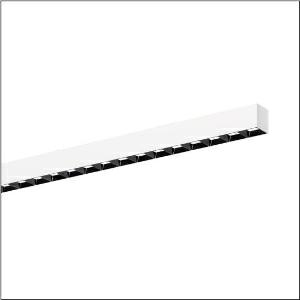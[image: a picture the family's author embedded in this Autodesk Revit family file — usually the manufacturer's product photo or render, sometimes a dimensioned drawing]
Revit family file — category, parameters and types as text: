
# Revit family: silica_r__21_51mx24tbt5w_c5f4
name_source: partatom
category: Lighting Fixtures
units: mm (PartAtom-declared; Revit-internal decimal feet)

## family parameters
Cut with Voids When Loaded = No
Host = Face
Light Source = No
Part Type = Normal
Room Calculation Point = No
Round Connector Dimension = Use Diameter
Shared = No

## types (1)
- --- (1 x LED, 4100 lm, 40.5 W, 6500K)
    Apparent Load = 41 VA
    CIE Flux Codes = 74 94 99 100 100
    Color Rendering = 80
    Color Temperature = 6500K
    Default Elevation = 1800 mm
    Description = Silica® 21, office luminaire, primary light control with darklight reflector, of PMMA, black, light emission: direct distribution, primary light characteristic: asymmetric, installation type: surface-mounted, LED, rated luminous flux: 4.100lm, luminous efficacy: 96lm/W, light colour: 8tw, colour temperature: 2700..6500K, control gear: ECG DALI, with terminal, 3+2-pole, max. 2.5mm², mains connection: 220..240V, AC, 50/60Hz, rated input power: 42.6W, luminaire housing, of aluminium, traffic white (RAL 9016), length: 1.504mm, width: 53mm, height: 53mm, protection rating (complete): IP20, insulation class (complete): insulation class I (protective earthing), certification: CE, permissible operating ambient temperature: 0..+35°C, standard: EN 50419, packaging unit: 1 piece
    Height = 0 mm  [stored 0 ft]
    Lamp = 1 x LED
    Lamp Light Flux = 4100 lm
    Lamp Power = 40.5 W
    Lamp count = 1
    Length = 1504 mm
    Luminous efficacy = 101 lm/W
    Manufacturer = Siteco
    ModVariant = No
    Model = 51MX24TBT5W
    Mounting Place = Ceiling
    Mounting Type = Recessed
    Number of Poles = 1
    OnlyDefault = Yes
    Power Factor = 1
    Product Name = Silica® 21
    Product group = office luminaire | ceiling recessed
    ProductGroupID = 401
    Protection Class = Protection class I
    Protection Degree = IP 20
    RLX_Detail_Level = 1
    RLX_Emergency_Light_Flux = 0 lm
    RLX_Emergency_Type = 0
    RLX_Emergency_Type_DB = No
    RlxData = <blob elided: 41769 chars, md5=2f8aff6a>
    Socket = socket
    Standby Power = 0 W
    System Light Flux = 4100 lm
    System Power = 41 W
    Type Comments = individual setting
    Type Image = l_1313592.jpg
    URL = http://relux.com
    VarID = @adj_089379
    Voltage = 0 V
    Weight = 0.00 kg
    Width = 53 mm

note: [stored X ft] marks values corroborated as IEEE doubles in the binary element streams (Revit-internal decimal feet)

## geometry (parser evidence)
native form markers: Blend x4, Sweep x9
no freeform markers — native parametric forms only
